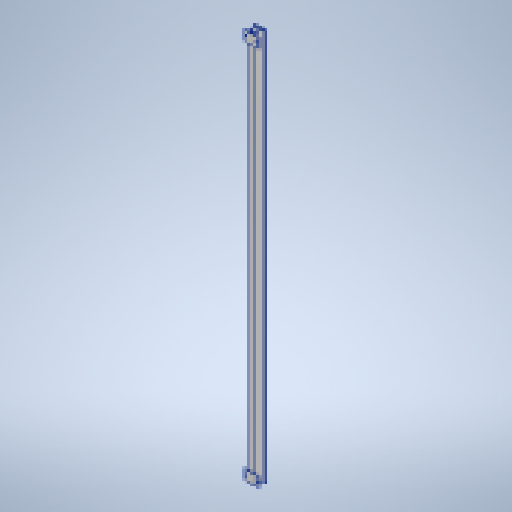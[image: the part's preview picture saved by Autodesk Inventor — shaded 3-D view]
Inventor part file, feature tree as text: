
AUTODESK INVENTOR PART (.ipt)
format: ipt  version: 2025 (Build 290162010, 162A)  size: 222,208 bytes
history: native  units: mm
features: sketch x3, extrude x2, projected_geometry x2, hole x1
ambient origin geometry x8: Origin, YZ Plane, XZ Plane, XY Plane, X Axis, Y Axis, Z Axis, Center Point
bodies: Volumenkörper1 (feature_tree)
feature tree (8):
  extrude  "Extrusion1"  Depth=2.0mm
  extrude  "Extrusion2"  Depth=20.0mm
  hole  "Bohrung1"  [1 undecoded]
  sketch  "Skizze1"  dims[d0=30.0mm d1=2.0mm]
  sketch  "Skizze2"  dims[d2=2.0mm d3=20.0mm]
  sketch  "Skizze3"  dims[d4=11.0mm d5=2.0mm d6=2.0mm d7=7.5mm d8=20.5mm d9=20.0mm d10=1000.0mm d11=0.0mm d12=7.5mm d13=24.0mm d15=2.0mm d16=0.0mm d19=6.0mm d21=4.0mm d22=4.0mm d23=15.0mm d24=24.0mm d25=4.0mm d26=4.0mm d27=6.0mm d28=6.0mm d29=5.5mm d30=6.0mm d31=10.4mm d32=2.0mm d33=90.0deg d34=8.0mm d35=20.594885mm d46=3.0mm d47=3.0mm d48=15.0mm]
  projected_geometry  "Projizierte Kontur1"
  projected_geometry  "Projizierte Kontur2"
note: 1 required parameter value undecoded (feature->parameter linkage not recoverable at this tier; creation-order binding heuristic only, values carry confidence <= 0.55)
